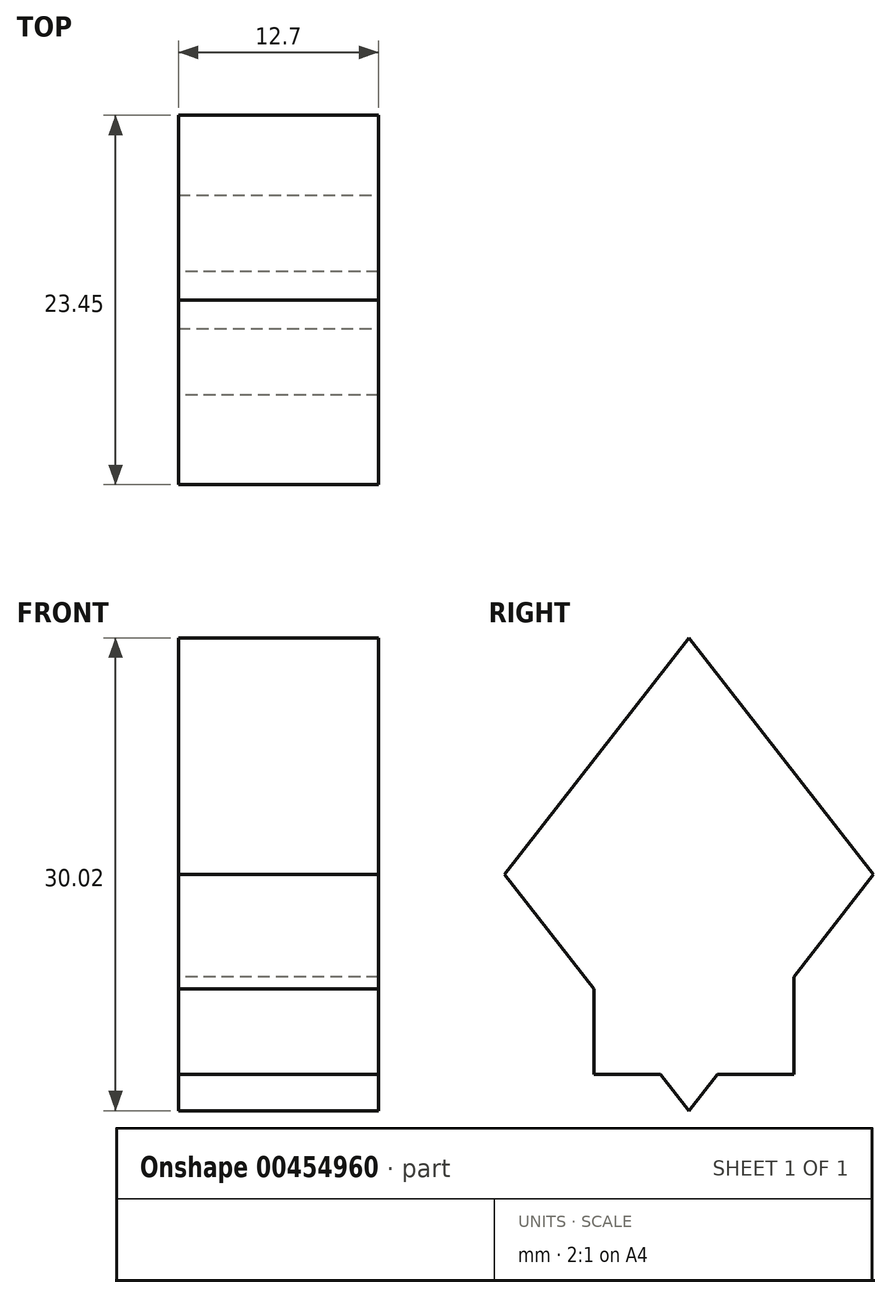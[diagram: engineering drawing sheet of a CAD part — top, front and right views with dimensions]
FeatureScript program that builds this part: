
annotation { "Feature Type Name" : "Feature", "Feature Type Description" : "" }
export const myFeature = defineFeature(function(context is Context, id is Id, definition is map)
    precondition{}
    {
        {
            var Q0;
            Q0=qCreatedBy(makeId("Top.planeOp"),FACE);
            var sketch = newSketch(context, id + "F0", { "sketchPlane" : qUnion([Q0])});
            skLineSegment(sketch, "E0.bottom", {"start": v(-49.04, 36.13) * mm, "end": v(-36.34, 36.13) * mm});
            skLineSegment(sketch, "E0.top", {"start": v(-49.04, 23.43) * mm, "end": v(-36.34, 23.43) * mm});
            skLineSegment(sketch, "E0.left", {"start": v(-49.04, 36.13) * mm, "end": v(-49.04, 23.43) * mm});
            skLineSegment(sketch, "E0.right", {"start": v(-36.34, 36.13) * mm, "end": v(-36.34, 23.43) * mm});
            skSolve(sketch);
        }
        {
            var Q0;
            Q0=makeQuery(id+"F0.imprint","IMPRINT",FACE,{"disambiguationData":[TD([[makeQuery(id+"F0.imprint","IMPRINT",EDGE,{"derivedFrom":sQuery(id+"F0.wireOp",EDGE,"E0.bottom")}),-1.0]])]});
            extrude(context, id + "F1", {"entities" : qUnion([Q0]), "depth" : 12.7 * mm});
        }
        {
            var Q0;
            Q0=makeQuery(id+"F1.opExtrude","SWEPT_FACE",FACE,{"disambiguationData":[OSD([sQuery(id+"F0.wireOp",EDGE,"E0.right")])]});
            var sketch = newSketch(context, id + "F2", { "sketchPlane" : qUnion([Q0])});
            skLineSegment(sketch, "E1", {"start": v(23.43, 12.7) * mm, "end": v(17.76, 12.7) * mm});
            skLineSegment(sketch, "E2", {"start": v(17.76, 12.7) * mm, "end": v(41.2, 12.7) * mm});
            skLineSegment(sketch, "E3", {"start": v(41.2, 12.7) * mm, "end": v(29.48, 27.71) * mm});
            skLineSegment(sketch, "E4", {"start": v(17.76, 12.7) * mm, "end": v(29.48, 27.71) * mm});
            skSolve(sketch);
        }
        {
            var Q0;
            {var subQ0=sQuery(id+"F2.wireOp",EDGE,"E3");Q0=makeQuery(id+"F2.imprint","IMPRINT",FACE,{"disambiguationData":[TD([[makeQuery(id+"F2.imprint","IMPRINT",EDGE,{"derivedFrom":subQ0}),1.0]])]});}
            extrude(context, id + "F3", {"entities" : qUnion([Q0]), "operationType" : NewBodyOperationType.ADD, "oppositeDirection" : true, "depth" : 12.7 * mm});
        }
        {
            var Q0;
            Q0=makeQuery(id+"F3.opExtrude","SWEPT_FACE",FACE,{"disambiguationData":[OSD([sQuery(id+"F2.wireOp",EDGE,"E4")])]});
            var Q1;
            Q1=makeQuery(id+"F3.opExtrude","CAP_EDGE",EDGE,{"disambiguationData":[OSD([sQuery(id+"F2.wireOp",EDGE,"E3")])],"isStart":false});
            sweep(context, id + "F4", {"operationType" : NewBodyOperationType.ADD, "profiles" : qUnion([Q0]), "path" : qUnion([Q1])});
        }
    });
